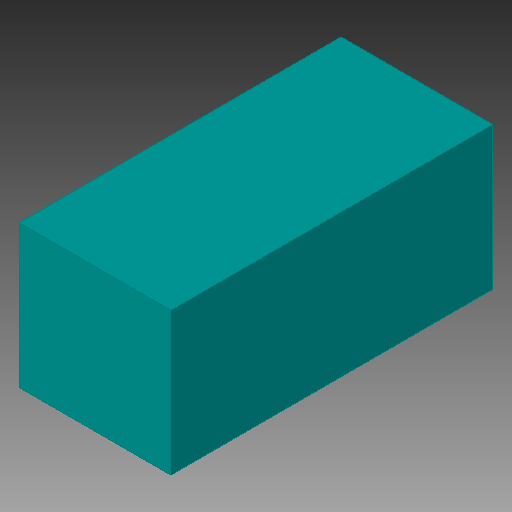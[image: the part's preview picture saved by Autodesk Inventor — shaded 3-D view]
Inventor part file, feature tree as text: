
AUTODESK INVENTOR PART (.ipt)
format: ipt  version: 2018 (Build 220112000, 112)  size: 80,384 bytes
history: native  units: in
note: dims shown in document units (in); Inventor stores cm internally (conversion verified against a paired STEP export)
features: other x1, extrude x1
ambient origin geometry x8: Origin, YZ Plane, XZ Plane, XY Plane, X Axis, Y Axis, Z Axis, Center Point
bodies: Solid1 (feature_tree)
feature tree (2):
  other  "MS_TM, MS_TM_158"
  extrude  "Extrusion1"  Depth=0.0394in TaperAngle=0.0deg
